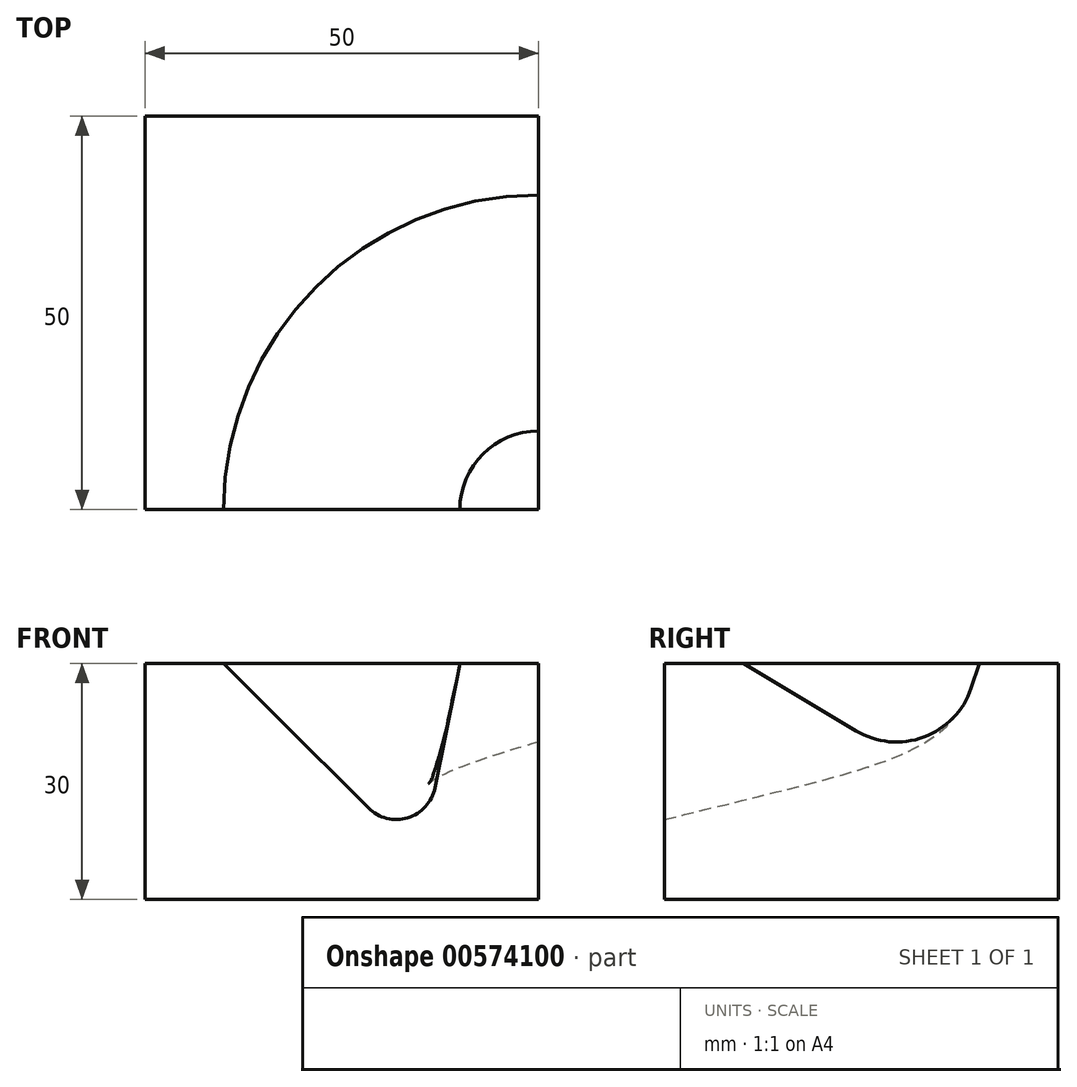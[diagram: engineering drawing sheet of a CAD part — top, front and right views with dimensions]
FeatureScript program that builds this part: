
annotation { "Feature Type Name" : "Feature", "Feature Type Description" : "" }
export const myFeature = defineFeature(function(context is Context, id is Id, definition is map)
    precondition{}
    {
        {
            var Q0;
            Q0=qCreatedBy(makeId("Top.planeOp"),FACE);
            var sketch = newSketch(context, id + "F0", { "sketchPlane" : qUnion([Q0])});
            skLineSegment(sketch, "E0.bottom", {"start": v(0, 0) * mm, "end": v(-50, 0) * mm});
            skLineSegment(sketch, "E0.top", {"start": v(0, 50) * mm, "end": v(-50, 50) * mm});
            skLineSegment(sketch, "E0.left", {"start": v(0, 0) * mm, "end": v(0, 50) * mm});
            skLineSegment(sketch, "E0.right", {"start": v(-50, 0) * mm, "end": v(-50, 50) * mm});
            skSolve(sketch);
        }
        {
            var Q0;
            Q0=makeQuery(id+"F0.imprint","IMPRINT",FACE,{"disambiguationData":[TD([[makeQuery(id+"F0.imprint","IMPRINT",EDGE,{"derivedFrom":sQuery(id+"F0.wireOp",EDGE,"E0.bottom")}),-1.0]])]});
            extrude(context, id + "F1", {"entities" : qUnion([Q0]), "depth" : 30 * mm, "offsetDistance" : 25 * mm});
        }
        {
            var Q0;
            Q0=makeQuery(id+"F1.opExtrude","SWEPT_FACE",FACE,{"disambiguationData":[OSD([sQuery(id+"F0.wireOp",EDGE,"E0.bottom")])]});
            var sketch = newSketch(context, id + "F2", { "sketchPlane" : qUnion([Q0])});
            skLineSegment(sketch, "E1", {"start": v(-40, 30) * mm, "end": v(-21.6, 11.6) * mm});
            skArc(sketch, "E2", {"start": v(-21.6, 11.6) * mm, "mid": v(-16.62, 10.36) * mm, "end": v(-13.17, 14.16) * mm});
            skLineSegment(sketch, "E3", {"start": v(-13.17, 14.16) * mm, "end": v(-10, 30) * mm});
            skPoint(sketch, "E4.orphan", {"position": v(-15, 5) * mm});
            skSolve(sketch);
        }
        {
            var Q0;
            Q0=makeQuery(id+"F1.opExtrude","CAP_FACE",FACE,{"disambiguationData":[OSD([sQuery(id+"F0.wireOp",EDGE,"E0.bottom"),sQuery(id+"F0.wireOp",EDGE,"E0.top"),sQuery(id+"F0.wireOp",EDGE,"E0.left"),sQuery(id+"F0.wireOp",EDGE,"E0.right")])],"isStart":false});
            var sketch = newSketch(context, id + "F3", { "sketchPlane" : qUnion([Q0])});
            skArc(sketch, "E5", {"start": v(-10, 0) * mm, "mid": v(-7.07, 7.07) * mm, "end": v(0, 10) * mm});
            skArc(sketch, "E6", {"start": v(-40, 0) * mm, "mid": v(-28.28, 28.28) * mm, "end": v(0, 40) * mm});
            skSolve(sketch);
        }
        {
            var Q0;
            Q0=makeQuery(id+"F1.opExtrude","SWEPT_FACE",FACE,{"disambiguationData":[OSD([sQuery(id+"F0.wireOp",EDGE,"E0.left")])]});
            var sketch = newSketch(context, id + "F4", { "sketchPlane" : qUnion([Q0])});
            skLineSegment(sketch, "E7", {"start": v(10, 30) * mm, "end": v(24.31, 21.41) * mm});
            skLineSegment(sketch, "E8", {"start": v(38.94, 26.83) * mm, "end": v(40, 30) * mm});
            skArc(sketch, "E9", {"start": v(24.31, 21.41) * mm, "mid": v(32.92, 20.6) * mm, "end": v(38.94, 26.83) * mm});
            skPoint(sketch, "E10.orphan", {"position": v(35, 15) * mm});
            skSolve(sketch);
        }
        {
            var Q1;
            Q1=makeQuery(id+"F2.imprint","IMPRINT",FACE,{"disambiguationData":[TD([[makeQuery(id+"F2.imprint","IMPRINT",EDGE,{"derivedFrom":sQuery(id+"F2.wireOp",EDGE,"E2")}),1.0]])]});
            var Q2;
            {var subQ0=sQuery(id+"F4.wireOp",EDGE,"E7");Q2=makeQuery(id+"F4.imprint","IMPRINT",FACE,{"disambiguationData":[TD([[makeQuery(id+"F4.imprint","IMPRINT",EDGE,{"derivedFrom":subQ0}),1.0]])]});}
            var Q3;
            Q3=sQuery(id+"F3.wireOp",EDGE,"E5");
            var Q4;
            Q4=sQuery(id+"F3.wireOp",EDGE,"E6");
            loft(context, id + "F5", {"operationType" : NewBodyOperationType.REMOVE, "addGuides" : true, "sheetProfilesArray" : [{ "sheetProfileEntities" : qUnion([Q1]) }, { "sheetProfileEntities" : qUnion([Q2]) }], "guidesArray" : [{ "guideEntities" : qUnion([Q3]), "guideDerivativeType" : LoftGuideDerivativeType.DEFAULT, "guideDerivativeMagnitude" : 1 }, { "guideEntities" : qUnion([Q4]), "guideDerivativeType" : LoftGuideDerivativeType.DEFAULT, "guideDerivativeMagnitude" : 1 }]});
        }
    });
